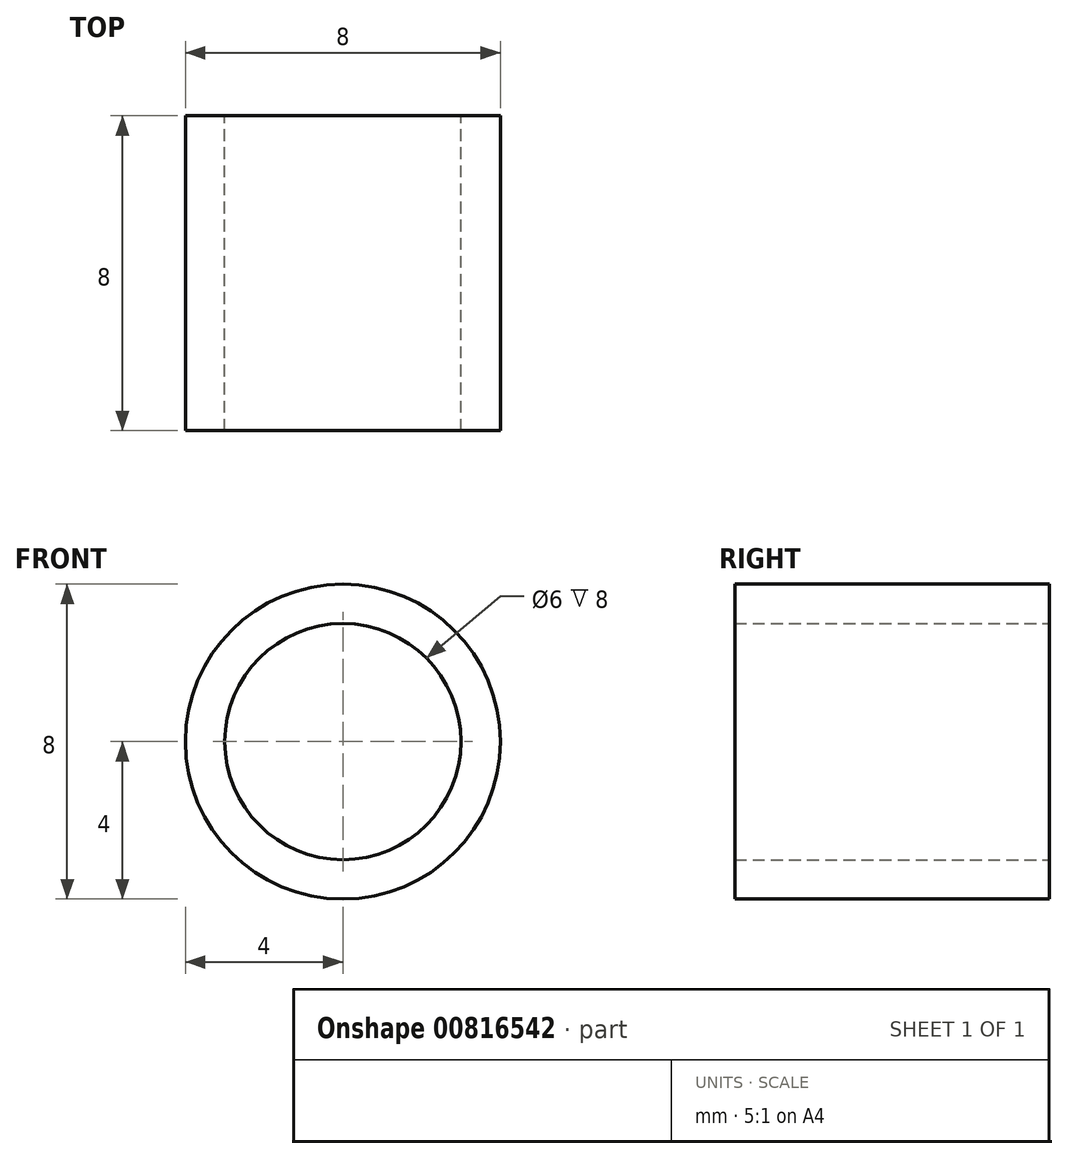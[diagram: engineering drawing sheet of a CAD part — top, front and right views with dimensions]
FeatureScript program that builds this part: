
annotation { "Feature Type Name" : "Feature", "Feature Type Description" : "" }
export const myFeature = defineFeature(function(context is Context, id is Id, definition is map)
    precondition{}
    {
        {
            var Q0;
            Q0=qCreatedBy(makeId("Front.planeOp"),FACE);
            var sketch = newSketch(context, id + "F0", { "sketchPlane" : qUnion([Q0])});
            skCircle(sketch, "E0", {"center": v(0, 0) * mm, "radius": 3 * mm});
            skCircle(sketch, "E1", {"center": v(0, 0) * mm, "radius": 4 * mm});
            skSolve(sketch);
        }
        {
            var Q0;
            Q0 = qSketchRegion(id + "F0", true);
            extrude(context, id + "F1", {"entities" : qUnion([Q0]), "depth" : 8 * mm, "offsetDistance" : 25 * mm});
        }
    });
